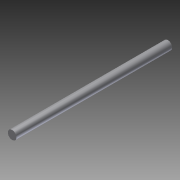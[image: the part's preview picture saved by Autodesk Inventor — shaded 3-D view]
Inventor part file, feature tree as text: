
AUTODESK INVENTOR PART (.ipt)
format: ipt  version: 2012 (Build 160160000, 160)  size: 66,048 bytes
history: native  units: in
note: dims shown in document units (in); Inventor stores cm internally (conversion verified against a paired STEP export)
features: extrude x1, sketch x1
ambient origin geometry x8: Origin, YZ Plane, XZ Plane, XY Plane, X Axis, Y Axis, Z Axis, Center Point
bodies: Solid1 (feature_tree)
feature tree (2):
  extrude  "Extrusion1"  Depth=6.75in TaperAngle=0.0deg
  sketch  "Sketch1"  dims[d0=0.375in d1=6.75in d2=0.0in]
